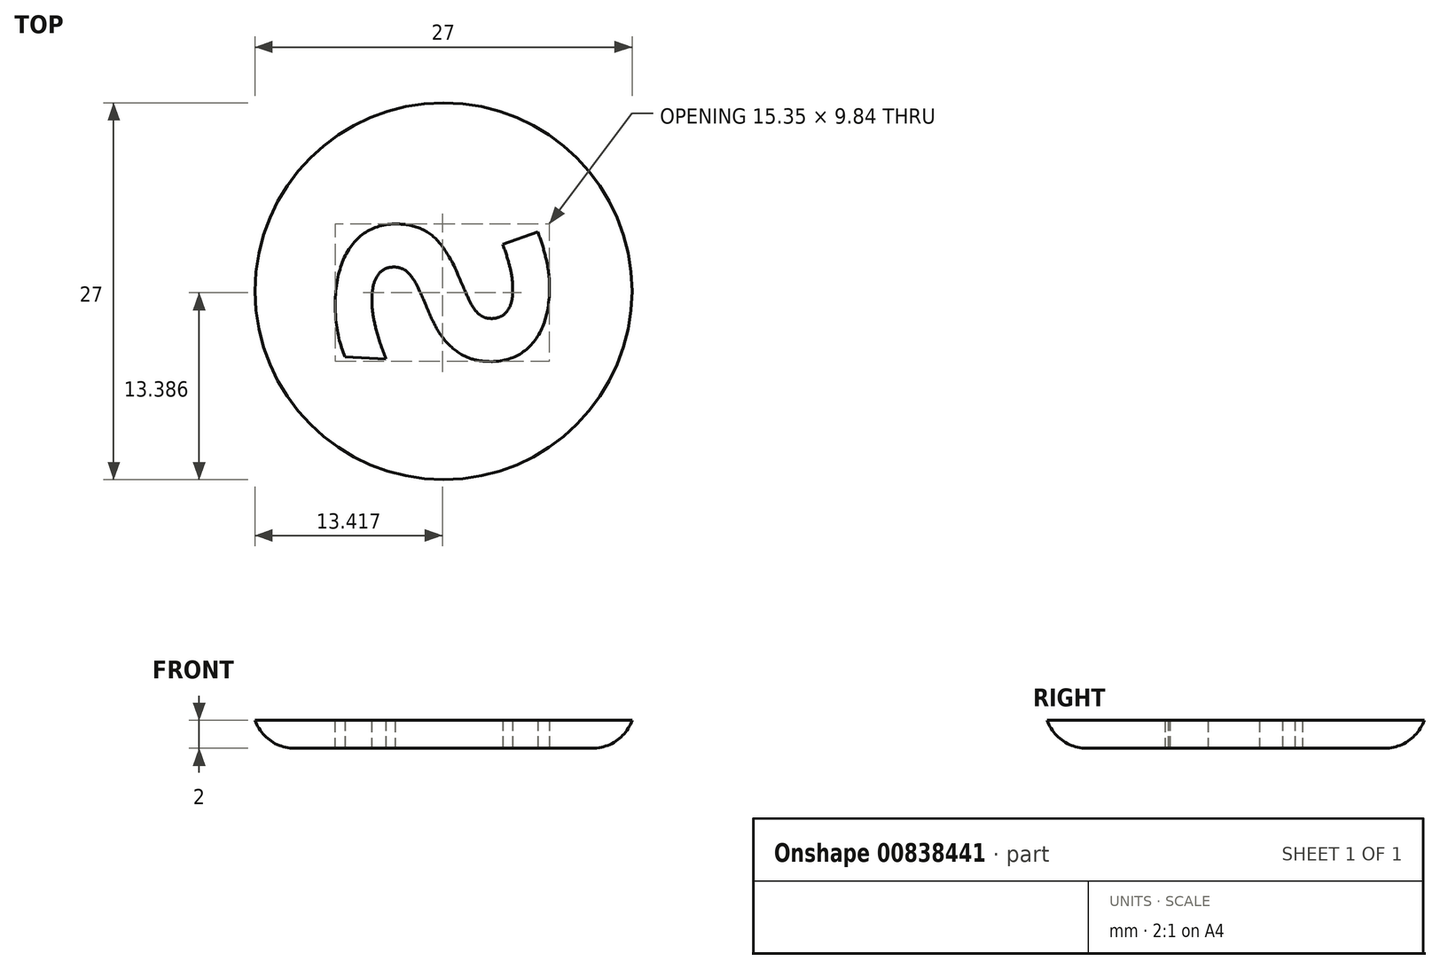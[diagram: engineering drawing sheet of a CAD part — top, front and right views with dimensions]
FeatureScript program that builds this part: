
annotation { "Feature Type Name" : "Feature", "Feature Type Description" : "" }
export const myFeature = defineFeature(function(context is Context, id is Id, definition is map)
    precondition{}
    {
        {
            var Q0;
            Q0=qCreatedBy(makeId("Top.planeOp"),FACE);
            var sketch = newSketch(context, id + "F0", { "sketchPlane" : qUnion([Q0])});
            skCircle(sketch, "E0", {"center": v(0, 0) * mm, "radius": 13.5 * mm});
            skSolve(sketch);
        }
        {
            var Q0;
            Q0 = qSketchRegion(id + "F0", true);
            extrude(context, id + "F1", {"entities" : qUnion([Q0]), "depth" : 2 * mm, "offsetDistance" : 25 * mm});
        }
        {
            var Q0;
            Q0=makeQuery(id+"F1.opExtrude","CAP_EDGE",EDGE,{"disambiguationData":[OSD([sQuery(id+"F0.wireOp",EDGE,"E0")])],"isStart":true});
            fillet(context, id + "F2", {"entities" : qUnion([Q0]), "radius" : 3 * mm, "tangentPropagation" : true, "allowEdgeOverflow" : false});
        }
        {
            var Q0;
            Q0=makeQuery(id+"F1.opExtrude","CAP_FACE",FACE,{"disambiguationData":[OSD([sQuery(id+"F0.wireOp",EDGE,"E0")])],"isStart":true});
            var sketch = newSketch(context, id + "F3", { "sketchPlane" : qUnion([Q0])});
            skText(sketch, "E1", { "text": "S", "fontName": "OpenSans-Bold.ttf"});
            const initialGuessF3  = {"E1": [-0.00779, 0.00563, 0.049, -0.9988, 0.015]};
            skSetInitialGuess(sketch, initialGuessF3);
            skSolve(sketch);
        }
        {
            var Q0;
            Q0 = qSketchRegion(id + "F3", true);
            extrude(context, id + "F4", {"entities" : qUnion([Q0]), "operationType" : NewBodyOperationType.REMOVE, "oppositeDirection" : true, "depth" : 2 * mm, "offsetDistance" : 25 * mm});
        }
    });
